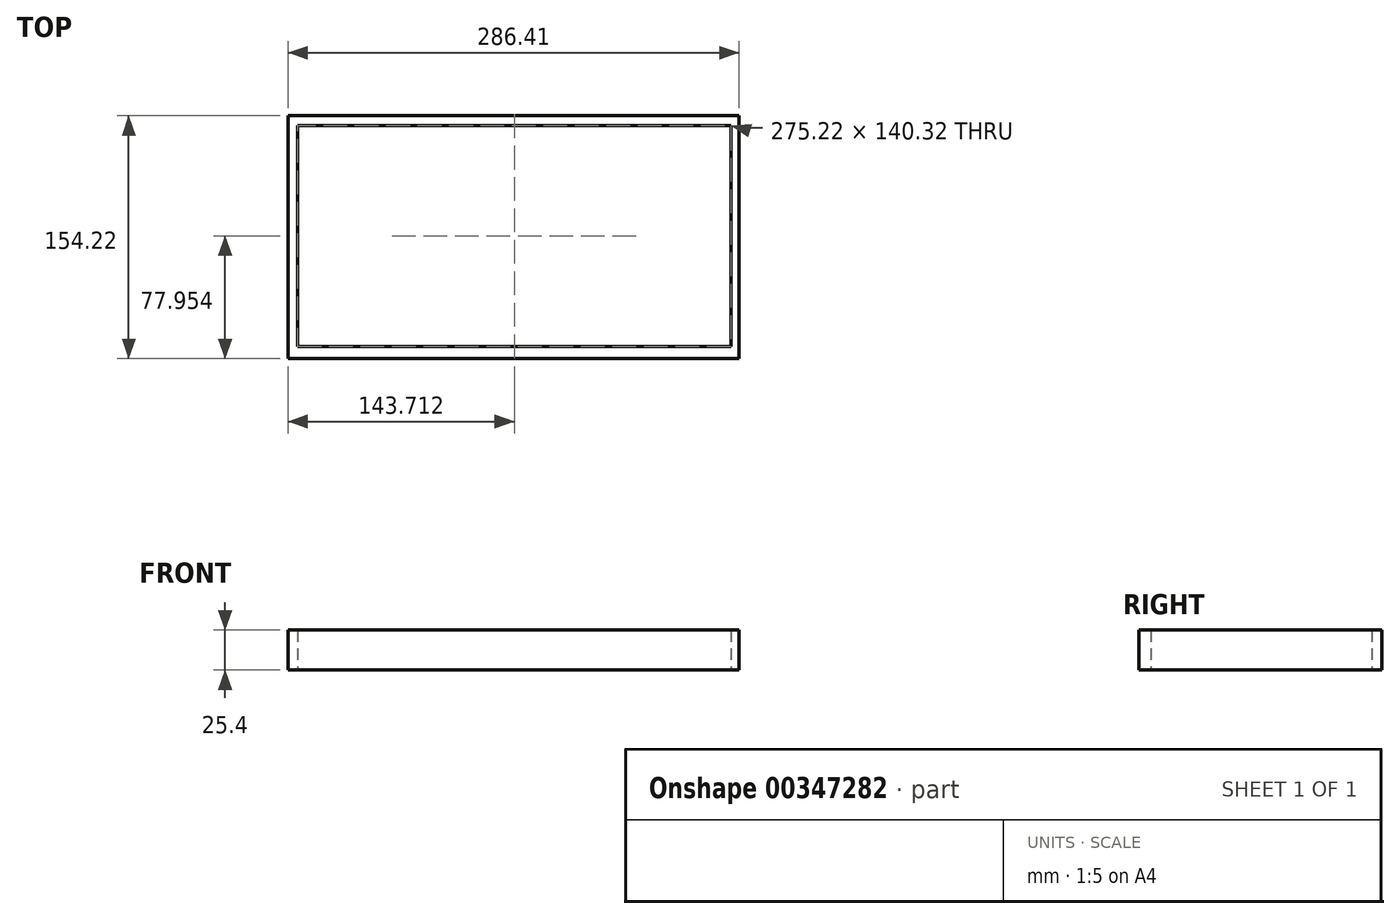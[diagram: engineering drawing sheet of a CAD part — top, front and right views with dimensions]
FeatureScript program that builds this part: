
annotation { "Feature Type Name" : "Feature", "Feature Type Description" : "" }
export const myFeature = defineFeature(function(context is Context, id is Id, definition is map)
    precondition{}
    {
        {
            var Q0;
            Q0=qCreatedBy(makeId("Top.planeOp"),FACE);
            var sketch = newSketch(context, id + "F0", { "sketchPlane" : qUnion([Q0])});
            skLineSegment(sketch, "E0.bottom", {"start": v(-142.73, 78.06) * mm, "end": v(143.68, 78.06) * mm});
            skLineSegment(sketch, "E0.top", {"start": v(-142.73, -76.16) * mm, "end": v(143.68, -76.16) * mm});
            skLineSegment(sketch, "E0.left", {"start": v(-142.73, 78.06) * mm, "end": v(-142.73, -76.16) * mm});
            skLineSegment(sketch, "E0.right", {"start": v(143.68, 78.06) * mm, "end": v(143.68, -76.16) * mm});
            skLineSegment(sketch, "E1.bottom", {"start": v(-136.63, 71.95) * mm, "end": v(138.6, 71.95) * mm});
            skLineSegment(sketch, "E1.top", {"start": v(-136.63, -68.37) * mm, "end": v(138.6, -68.37) * mm});
            skLineSegment(sketch, "E1.left", {"start": v(-136.63, 71.95) * mm, "end": v(-136.63, -68.37) * mm});
            skLineSegment(sketch, "E1.right", {"start": v(138.6, 71.95) * mm, "end": v(138.6, -68.37) * mm});
            skSolve(sketch);
        }
        {
            var Q0;
            Q0 = qSketchRegion(id + "F0", true);
            extrude(context, id + "F1", {"entities" : qUnion([Q0]), "depth" : 25.4 * mm});
        }
    });
